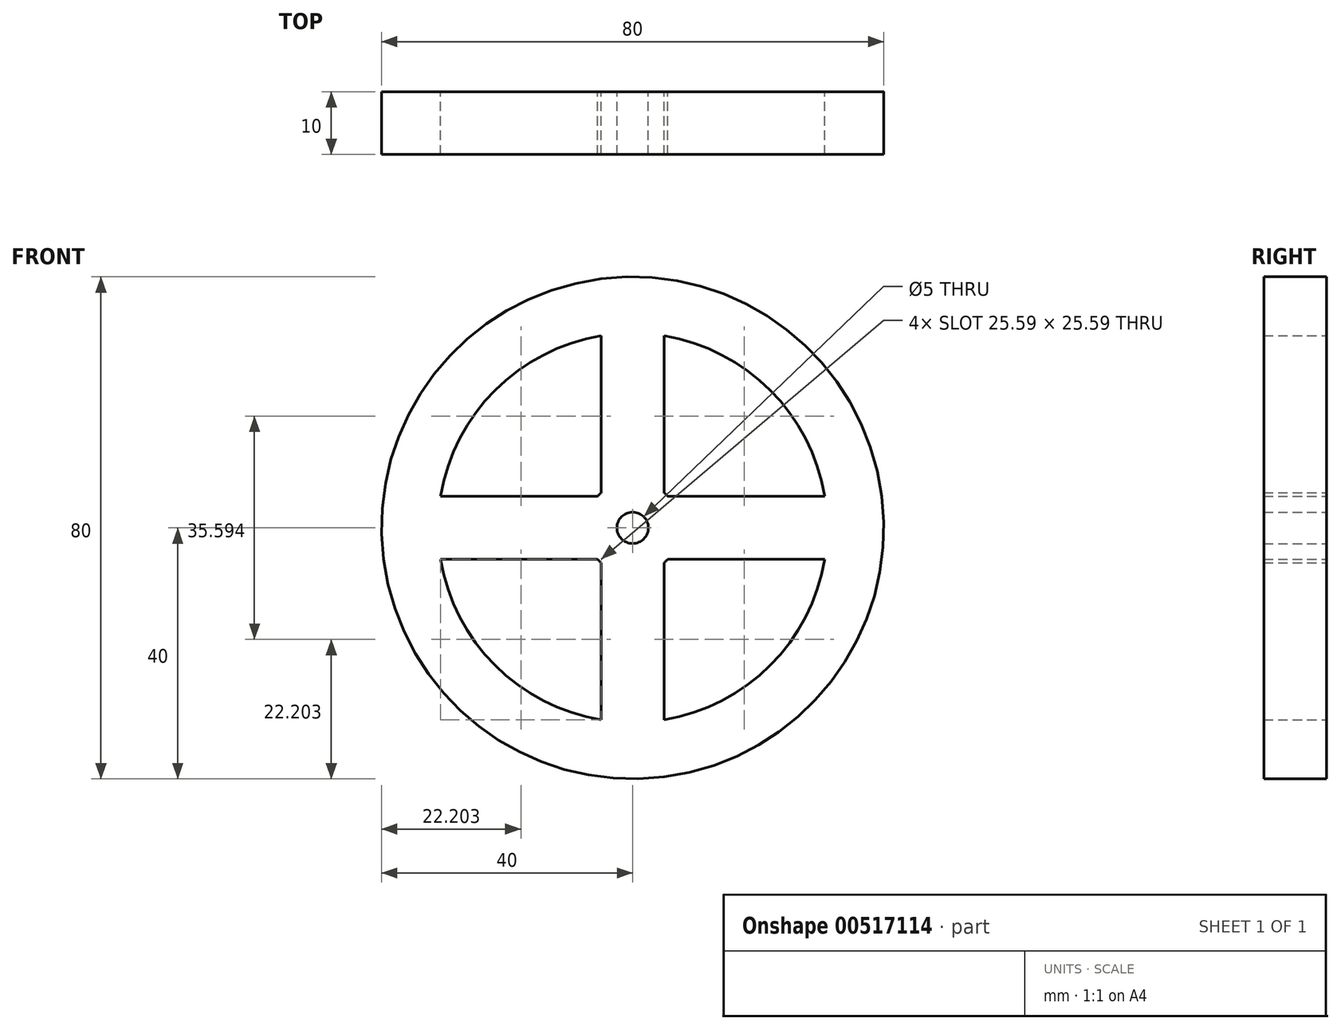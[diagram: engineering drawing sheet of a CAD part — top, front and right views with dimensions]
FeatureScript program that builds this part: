
annotation { "Feature Type Name" : "Feature", "Feature Type Description" : "" }
export const myFeature = defineFeature(function(context is Context, id is Id, definition is map)
    precondition{}
    {
        {
            var Q0;
            Q0=qCreatedBy(makeId("Front.planeOp"),FACE);
            var sketch = newSketch(context, id + "F0", { "sketchPlane" : qUnion([Q0])});
            skCircle(sketch, "E0", {"center": v(0, 0) * mm, "radius": 40 * mm});
            skArc(sketch, "E1", {"start": v(-5, 30.6) * mm, "mid": v(0, -31) * mm, "end": v(5, 30.6) * mm});
            skArc(sketch, "E2", {"start": v(-5, 5.6) * mm, "mid": v(-5.3, 5.3) * mm, "end": v(-5.6, 5) * mm});
            skCircle(sketch, "E3", {"center": v(0, 0) * mm, "radius": 2.5 * mm});
            skLineSegment(sketch, "E4", {"start": v(2.5, 0) * mm, "end": v(40, 0) * mm});
            skLineSegment(sketch, "E5", {"start": v(0, 0) * mm, "end": v(0, -47.35) * mm});
            skLineSegment(sketch, "E6", {"start": v(0, 0) * mm, "end": v(0, 7.5) * mm});
            skLineSegment(sketch, "E7.0", {"start": v(5, 5.6) * mm, "end": v(5, 30.6) * mm});
            skLineSegment(sketch, "E8.0", {"start": v(-5, 5.6) * mm, "end": v(-5, 30.6) * mm});
            skLineSegment(sketch, "E9.0", {"start": v(-5, -5.6) * mm, "end": v(-5, -47.35) * mm});
            skLineSegment(sketch, "E10.0", {"start": v(5, -5.6) * mm, "end": v(5, -47.35) * mm});
            skLineSegment(sketch, "E11.0", {"start": v(5.6, 5) * mm, "end": v(39.69, 5) * mm});
            skLineSegment(sketch, "E12.0", {"start": v(5.6, -5) * mm, "end": v(39.69, -5) * mm});
            skArc(sketch, "E13.trimOffspring", {"start": v(5.6, 5) * mm, "mid": v(5.3, 5.3) * mm, "end": v(5, 5.6) * mm});
            skArc(sketch, "E14.trimOffspring", {"start": v(5, -5.6) * mm, "mid": v(5.3, -5.3) * mm, "end": v(5.6, -5) * mm});
            skArc(sketch, "E15.trimOffspring", {"start": v(-5.6, -5) * mm, "mid": v(-5.3, -5.3) * mm, "end": v(-5, -5.6) * mm});
            skLineSegment(sketch, "E16.trimOffspring", {"start": v(-5.6, 5) * mm, "end": v(-30.6, 5) * mm});
            skLineSegment(sketch, "E17.trimOffspring", {"start": v(-5.6, -5) * mm, "end": v(-39.69, -5) * mm});
            skPoint(sketch, "E18.start.orphan", {"position": v(0.88, 0) * mm});
            skSolve(sketch);
        }
        {
            var Q0;
            Q0=makeQuery(id+"F0.imprint","IMPRINT",FACE,{"disambiguationData":[TD([[makeQuery(id+"F0.imprint","IMPRINT",EDGE,{"derivedFrom":sQuery(id+"F0.wireOp",EDGE,"E2")}),1.0]])]});
            var Q1;
            {var subQ0=sQuery(id+"F0.wireOp",EDGE,"E4");var subQ1=sQuery(id+"F0.wireOp",EDGE,"E0");var subQ2=makeQuery(id+"F0.imprint","INTERSECT",VERTEX,{"derivedFrom":[subQ1,subQ0]});Q1=makeQuery(id+"F0.imprint","IMPRINT",FACE,{"disambiguationData":[TD([[makeQuery(id+"F0.imprint","IMPRINT",EDGE,{"disambiguationData":[TD([[subQ2,-1.0]])],"derivedFrom":subQ1}),1.0]])]});}
            var Q2;
            {var subQ0=sQuery(id+"F0.wireOp",EDGE,"E4");var subQ1=sQuery(id+"F0.wireOp",EDGE,"E0");var subQ2=makeQuery(id+"F0.imprint","INTERSECT",VERTEX,{"derivedFrom":[subQ1,subQ0]});Q2=makeQuery(id+"F0.imprint","IMPRINT",FACE,{"disambiguationData":[TD([[makeQuery(id+"F0.imprint","IMPRINT",EDGE,{"disambiguationData":[TD([[subQ2,1.0]])],"derivedFrom":subQ1}),1.0]])]});}
            var Q3;
            {var subQ0=sQuery(id+"F0.wireOp",EDGE,"E12.0");var subQ1=sQuery(id+"F0.wireOp",EDGE,"E0");var subQ2=makeQuery(id+"F0.imprint","INTERSECT",VERTEX,{"derivedFrom":[subQ1,subQ0]});Q3=makeQuery(id+"F0.imprint","IMPRINT",FACE,{"disambiguationData":[TD([[makeQuery(id+"F0.imprint","IMPRINT",EDGE,{"disambiguationData":[TD([[subQ2,1.0]])],"derivedFrom":subQ1}),1.0]])]});}
            var Q4;
            {var subQ0=sQuery(id+"F0.wireOp",EDGE,"E17.trimOffspring");var subQ1=sQuery(id+"F0.wireOp",EDGE,"E0");var subQ2=makeQuery(id+"F0.imprint","INTERSECT",VERTEX,{"derivedFrom":[subQ1,subQ0]});Q4=makeQuery(id+"F0.imprint","IMPRINT",FACE,{"disambiguationData":[TD([[makeQuery(id+"F0.imprint","IMPRINT",EDGE,{"disambiguationData":[TD([[subQ2,-1.0]])],"derivedFrom":subQ1}),1.0]])]});}
            var Q5;
            {var subQ0=sQuery(id+"F0.wireOp",EDGE,"E9.0");var subQ1=sQuery(id+"F0.wireOp",EDGE,"E0");var subQ2=makeQuery(id+"F0.imprint","INTERSECT",VERTEX,{"derivedFrom":[subQ1,subQ0]});Q5=makeQuery(id+"F0.imprint","IMPRINT",FACE,{"disambiguationData":[TD([[makeQuery(id+"F0.imprint","IMPRINT",EDGE,{"disambiguationData":[TD([[subQ2,-1.0]])],"derivedFrom":subQ1}),1.0]])]});}
            var Q6;
            {var subQ0=sQuery(id+"F0.wireOp",EDGE,"E5");var subQ1=sQuery(id+"F0.wireOp",EDGE,"E0");var subQ2=makeQuery(id+"F0.imprint","INTERSECT",VERTEX,{"derivedFrom":[subQ1,subQ0]});Q6=makeQuery(id+"F0.imprint","IMPRINT",FACE,{"disambiguationData":[TD([[makeQuery(id+"F0.imprint","IMPRINT",EDGE,{"disambiguationData":[TD([[subQ2,-1.0]])],"derivedFrom":subQ1}),1.0]])]});}
            var Q7;
            {var subQ7=sQuery(id+"F0.wireOp",EDGE,"E14.trimOffspring");Q7=makeQuery(id+"F0.imprint","IMPRINT",FACE,{"disambiguationData":[TD([[makeQuery(id+"F0.imprint","IMPRINT",EDGE,{"derivedFrom":subQ7}),1.0]])]});}
            extrude(context, id + "F1", {"entities" : qUnion([Q0, Q1, Q2, Q3, Q4, Q5, Q6, Q7]), "depth" : 10 * mm, "offsetDistance" : 25 * mm});
        }
    });
